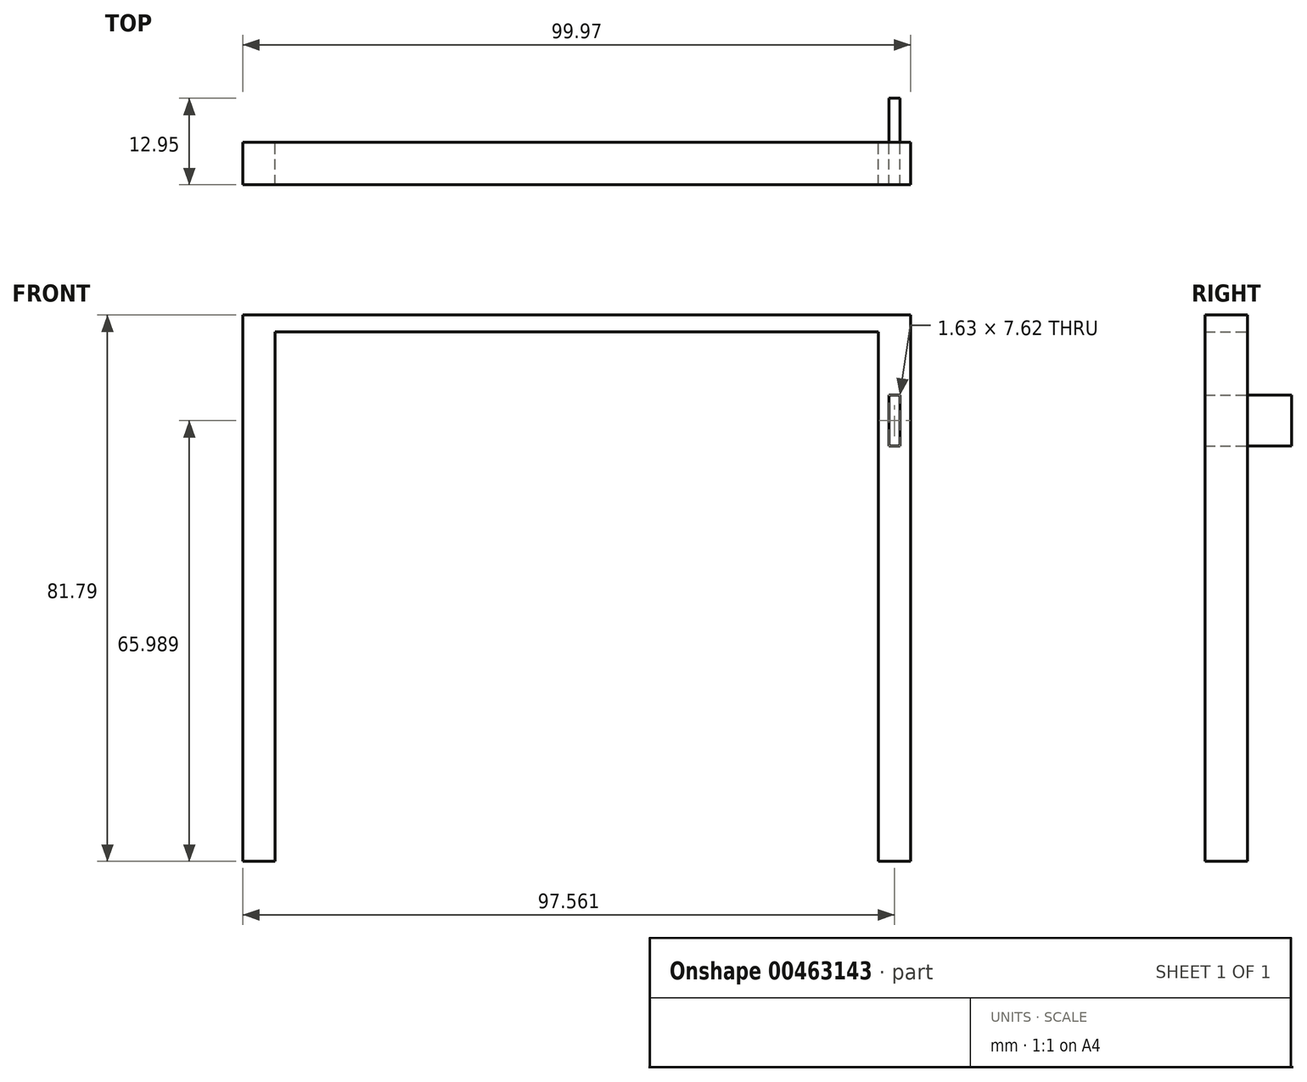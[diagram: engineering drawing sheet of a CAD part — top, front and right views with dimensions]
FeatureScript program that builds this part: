
annotation { "Feature Type Name" : "Feature", "Feature Type Description" : "" }
export const myFeature = defineFeature(function(context is Context, id is Id, definition is map)
    precondition{}
    {
        {
            var Q0;
            Q0=qCreatedBy(makeId("Front.planeOp"),FACE);
            var sketch = newSketch(context, id + "F0", { "sketchPlane" : qUnion([Q0])});
            skLineSegment(sketch, "E0.top", {"start": v(0, 81.79) * mm, "end": v(99.97, 81.79) * mm});
            skLineSegment(sketch, "E0.left", {"start": v(0, 0) * mm, "end": v(0, 81.79) * mm});
            skLineSegment(sketch, "E0.right", {"start": v(99.97, 0) * mm, "end": v(99.97, 81.79) * mm});
            skLineSegment(sketch, "E1", {"start": v(0, 0) * mm, "end": v(99.97, 0) * mm});
            skLineSegment(sketch, "E2.0", {"start": v(4.83, 79.25) * mm, "end": v(95.15, 79.25) * mm});
            skLineSegment(sketch, "E3.0", {"start": v(95.15, 0) * mm, "end": v(95.15, 79.25) * mm});
            skLineSegment(sketch, "E4.0", {"start": v(4.83, 0) * mm, "end": v(4.83, 79.25) * mm});
            skLineSegment(sketch, "E5", {"start": v(49.99, 79.25) * mm, "end": v(49.99, 0) * mm});
            skLineSegment(sketch, "E6", {"start": v(95.15, 40.9) * mm, "end": v(4.83, 40.9) * mm});
            skLineSegment(sketch, "E7.MirrorCS", {"start": v(95.15, 98.7) * mm, "end": v(4.83, 98.7) * mm});
            skLineSegment(sketch, "E8.bottom", {"start": v(98.37, 69.8) * mm, "end": v(96.75, 69.8) * mm});
            skLineSegment(sketch, "E8.top", {"start": v(98.37, 62.18) * mm, "end": v(96.75, 62.18) * mm});
            skLineSegment(sketch, "E8.left", {"start": v(98.37, 69.8) * mm, "end": v(98.37, 62.18) * mm});
            skLineSegment(sketch, "E8.right", {"start": v(96.75, 69.8) * mm, "end": v(96.75, 62.18) * mm});
            skSolve(sketch);
        }
        {
            var Q0;
            Q0=makeQuery(id+"F0.imprint","IMPRINT",FACE,{"disambiguationData":[TD([[makeQuery(id+"F0.imprint","IMPRINT",EDGE,{"derivedFrom":sQuery(id+"F0.wireOp",EDGE,"E0.top")}),-1.0]])]});
            extrude(context, id + "F1", {"entities" : qUnion([Q0]), "depth" : 6.35 * mm});
        }
        {
            var Q0;
            Q0=makeQuery(id+"F0.imprint","IMPRINT",FACE,{"disambiguationData":[TD([[makeQuery(id+"F0.imprint","IMPRINT",EDGE,{"derivedFrom":sQuery(id+"F0.wireOp",EDGE,"E8.bottom")}),1.0]])]});
            extrude(context, id + "F2", {"entities" : qUnion([Q0]), "depth" : 6.35 * mm});
        }
        {
            var Q0;
            Q0=makeQuery(id+"F0.imprint","IMPRINT",FACE,{"disambiguationData":[TD([[makeQuery(id+"F0.imprint","IMPRINT",EDGE,{"derivedFrom":sQuery(id+"F0.wireOp",EDGE,"E8.bottom")}),1.0]])]});
            extrude(context, id + "F3", {"entities" : qUnion([Q0]), "oppositeDirection" : true, "depth" : 6.6 * mm});
        }
    });
